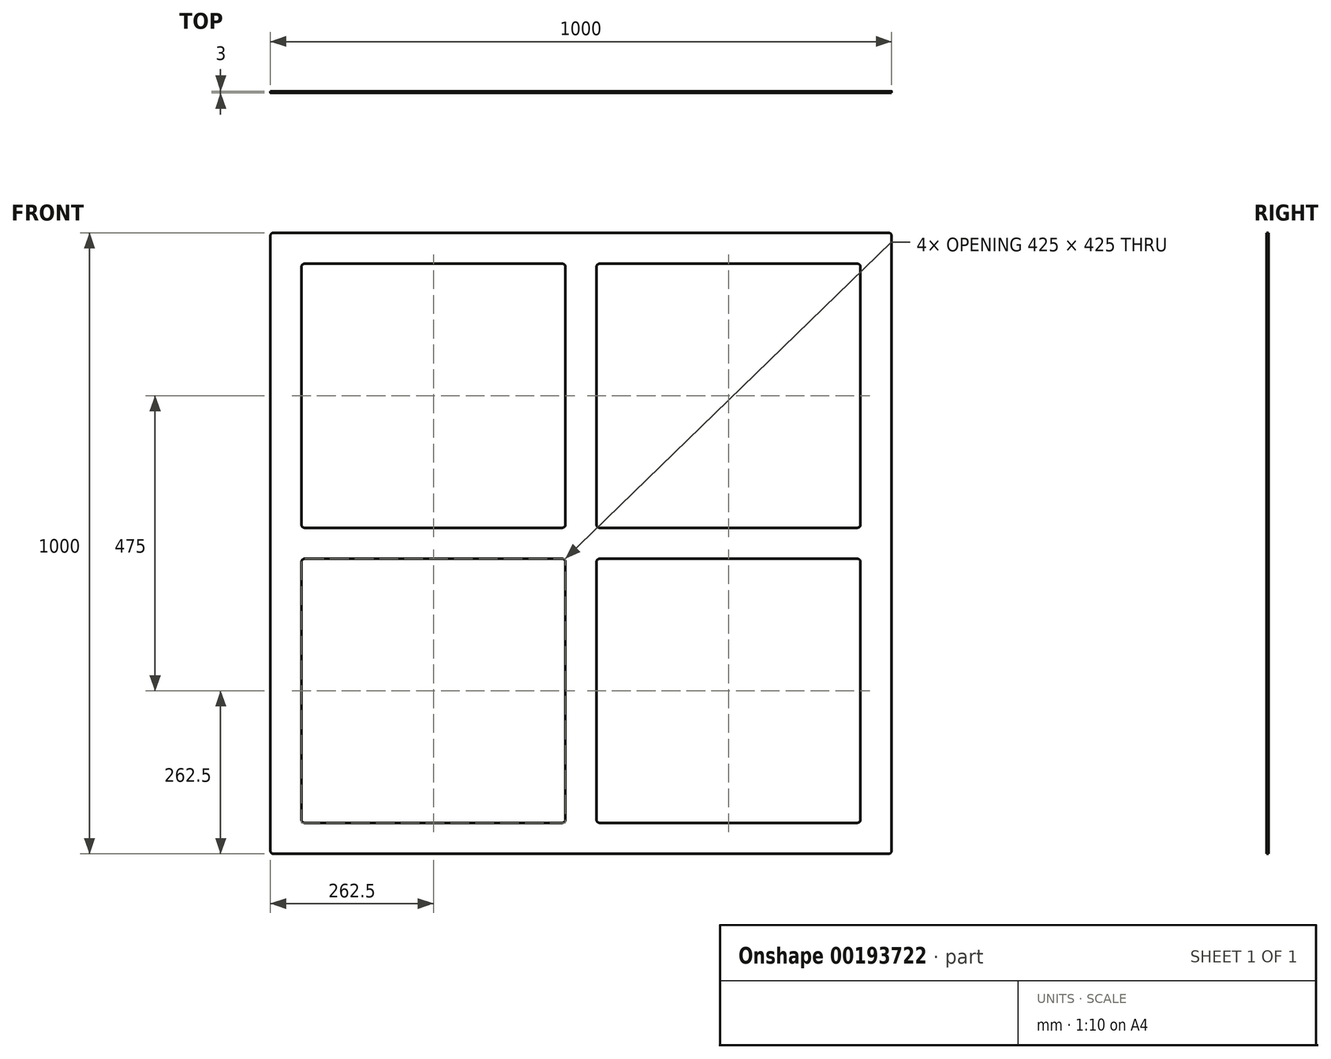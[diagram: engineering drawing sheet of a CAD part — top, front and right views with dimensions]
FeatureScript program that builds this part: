
annotation { "Feature Type Name" : "Feature", "Feature Type Description" : "" }
export const myFeature = defineFeature(function(context is Context, id is Id, definition is map)
    precondition{}
    {
        {
            var Q0;
            Q0=qCreatedBy(makeId("Front.planeOp"),FACE);
            var sketch = newSketch(context, id + "F0", { "sketchPlane" : qUnion([Q0])});
            skLineSegment(sketch, "E0.bottom", {"start": v(495, 500) * mm, "end": v(-495, 500) * mm});
            skLineSegment(sketch, "E0.top", {"start": v(495, -500) * mm, "end": v(-495, -500) * mm});
            skLineSegment(sketch, "E0.left", {"start": v(500, 495) * mm, "end": v(500, -495) * mm});
            skLineSegment(sketch, "E0.right", {"start": v(-500, 495) * mm, "end": v(-500, -495) * mm});
            skPoint(sketch, "E0.middle", {"position": v(0, 0) * mm});
            skLineSegment(sketch, "E1.bottom", {"start": v(-30, 25) * mm, "end": v(-445, 25) * mm});
            skLineSegment(sketch, "E1.top", {"start": v(-30, 450) * mm, "end": v(-445, 450) * mm});
            skLineSegment(sketch, "E1.left", {"start": v(-25, 30) * mm, "end": v(-25, 445) * mm});
            skLineSegment(sketch, "E1.right", {"start": v(-450, 30) * mm, "end": v(-450, 445) * mm});
            skPoint(sketch, "E1.middle", {"position": v(-237.5, 237.5) * mm});
            skLineSegment(sketch, "E2.0.1.0", {"start": v(-450, -445) * mm, "end": v(-450, -30) * mm});
            skLineSegment(sketch, "E2.0.1.1", {"start": v(-25, -445) * mm, "end": v(-25, -30) * mm});
            skLineSegment(sketch, "E2.0.1.2", {"start": v(-30, -25) * mm, "end": v(-445, -25) * mm});
            skPoint(sketch, "E2.0.1.3", {"position": v(-237.5, -237.5) * mm});
            skLineSegment(sketch, "E2.0.1.4", {"start": v(-30, -450) * mm, "end": v(-445, -450) * mm});
            skLineSegment(sketch, "E2.1.0.0", {"start": v(25, 30) * mm, "end": v(25, 445) * mm});
            skLineSegment(sketch, "E2.1.0.1", {"start": v(450, 30) * mm, "end": v(450, 445) * mm});
            skLineSegment(sketch, "E2.1.0.2", {"start": v(445, 450) * mm, "end": v(30, 450) * mm});
            skPoint(sketch, "E2.1.0.3", {"position": v(237.5, 237.5) * mm});
            skLineSegment(sketch, "E2.1.0.4", {"start": v(445, 25) * mm, "end": v(30, 25) * mm});
            skLineSegment(sketch, "E2.1.1.0", {"start": v(25, -445) * mm, "end": v(25, -30) * mm});
            skLineSegment(sketch, "E2.1.1.1", {"start": v(450, -445) * mm, "end": v(450, -30) * mm});
            skLineSegment(sketch, "E2.1.1.2", {"start": v(445, -25) * mm, "end": v(30, -25) * mm});
            skPoint(sketch, "E2.1.1.3", {"position": v(237.5, -237.5) * mm});
            skLineSegment(sketch, "E2.1.1.4", {"start": v(445, -450) * mm, "end": v(30, -450) * mm});
            skLineSegment(sketch, "E2.direction1", {"start": v(-450, 25) * mm, "end": v(25, 25) * mm, "construction": true});
            skLineSegment(sketch, "E2.direction2", {"start": v(-450, 25) * mm, "end": v(-450, -450) * mm, "construction": true});
            skPoint(sketch, "E3.visualSharp", {"position": v(-500, 500) * mm});
            skArc(sketch, "E3.filletArc", {"start": v(-495, 500) * mm, "mid": v(-498.54, 498.54) * mm, "end": v(-500, 495) * mm});
            skPoint(sketch, "E4.visualSharp", {"position": v(500, 500) * mm});
            skArc(sketch, "E4.filletArc", {"start": v(500, 495) * mm, "mid": v(498.54, 498.54) * mm, "end": v(495, 500) * mm});
            skPoint(sketch, "E5.visualSharp", {"position": v(500, -500) * mm});
            skArc(sketch, "E5.filletArc", {"start": v(495, -500) * mm, "mid": v(498.54, -498.54) * mm, "end": v(500, -495) * mm});
            skPoint(sketch, "E6.visualSharp", {"position": v(-500, -500) * mm});
            skArc(sketch, "E6.filletArc", {"start": v(-500, -495) * mm, "mid": v(-498.54, -498.54) * mm, "end": v(-495, -500) * mm});
            skPoint(sketch, "E7.visualSharp", {"position": v(-450, -450) * mm});
            skArc(sketch, "E7.filletArc", {"start": v(-450, -445) * mm, "mid": v(-448.54, -448.54) * mm, "end": v(-445, -450) * mm});
            skPoint(sketch, "E8.visualSharp", {"position": v(-25, -450) * mm});
            skArc(sketch, "E8.filletArc", {"start": v(-30, -450) * mm, "mid": v(-26.46, -448.54) * mm, "end": v(-25, -445) * mm});
            skPoint(sketch, "E9.visualSharp", {"position": v(450, -450) * mm});
            skArc(sketch, "E9.filletArc", {"start": v(445, -450) * mm, "mid": v(448.54, -448.54) * mm, "end": v(450, -445) * mm});
            skPoint(sketch, "E10.visualSharp", {"position": v(450, -25) * mm});
            skArc(sketch, "E10.filletArc", {"start": v(450, -30) * mm, "mid": v(448.54, -26.46) * mm, "end": v(445, -25) * mm});
            skPoint(sketch, "E11.visualSharp", {"position": v(25, -25) * mm});
            skArc(sketch, "E11.filletArc", {"start": v(30, -25) * mm, "mid": v(26.46, -26.46) * mm, "end": v(25, -30) * mm});
            skPoint(sketch, "E12.visualSharp", {"position": v(450, 450) * mm});
            skArc(sketch, "E12.filletArc", {"start": v(450, 445) * mm, "mid": v(448.54, 448.54) * mm, "end": v(445, 450) * mm});
            skPoint(sketch, "E13.visualSharp", {"position": v(450, 25) * mm});
            skArc(sketch, "E13.filletArc", {"start": v(445, 25) * mm, "mid": v(448.54, 26.46) * mm, "end": v(450, 30) * mm});
            skPoint(sketch, "E14.visualSharp", {"position": v(25, 25) * mm});
            skArc(sketch, "E14.filletArc", {"start": v(25, 30) * mm, "mid": v(26.46, 26.46) * mm, "end": v(30, 25) * mm});
            skPoint(sketch, "E15.visualSharp", {"position": v(25, 450) * mm});
            skArc(sketch, "E15.filletArc", {"start": v(30, 450) * mm, "mid": v(26.46, 448.54) * mm, "end": v(25, 445) * mm});
            skPoint(sketch, "E16.visualSharp", {"position": v(-25, 450) * mm});
            skArc(sketch, "E16.filletArc", {"start": v(-25, 445) * mm, "mid": v(-26.46, 448.54) * mm, "end": v(-30, 450) * mm});
            skPoint(sketch, "E17.visualSharp", {"position": v(-450, 450) * mm});
            skArc(sketch, "E17.filletArc", {"start": v(-445, 450) * mm, "mid": v(-448.54, 448.54) * mm, "end": v(-450, 445) * mm});
            skPoint(sketch, "E18.visualSharp", {"position": v(-450, 25) * mm});
            skArc(sketch, "E18.filletArc", {"start": v(-450, 30) * mm, "mid": v(-448.54, 26.46) * mm, "end": v(-445, 25) * mm});
            skPoint(sketch, "E19.visualSharp", {"position": v(-25, 25) * mm});
            skArc(sketch, "E19.filletArc", {"start": v(-30, 25) * mm, "mid": v(-26.46, 26.46) * mm, "end": v(-25, 30) * mm});
            skPoint(sketch, "E20.visualSharp", {"position": v(-450, -25) * mm});
            skArc(sketch, "E20.filletArc", {"start": v(-445, -25) * mm, "mid": v(-448.54, -26.46) * mm, "end": v(-450, -30) * mm});
            skPoint(sketch, "E21.visualSharp", {"position": v(-25, -25) * mm});
            skArc(sketch, "E21.filletArc", {"start": v(-25, -30) * mm, "mid": v(-26.46, -26.46) * mm, "end": v(-30, -25) * mm});
            skPoint(sketch, "E22.visualSharp", {"position": v(25, -450) * mm});
            skArc(sketch, "E22.filletArc", {"start": v(25, -445) * mm, "mid": v(26.46, -448.54) * mm, "end": v(30, -450) * mm});
            skSolve(sketch);
        }
        {
            var Q0;
            Q0=makeQuery(id+"F0.imprint","IMPRINT",FACE,{"disambiguationData":[TD([[makeQuery(id+"F0.imprint","IMPRINT",EDGE,{"derivedFrom":sQuery(id+"F0.wireOp",EDGE,"E0.bottom")}),1.0]])]});
            extrude(context, id + "F1", {"entities" : qUnion([Q0]), "depth" : 3 * mm});
        }
    });
